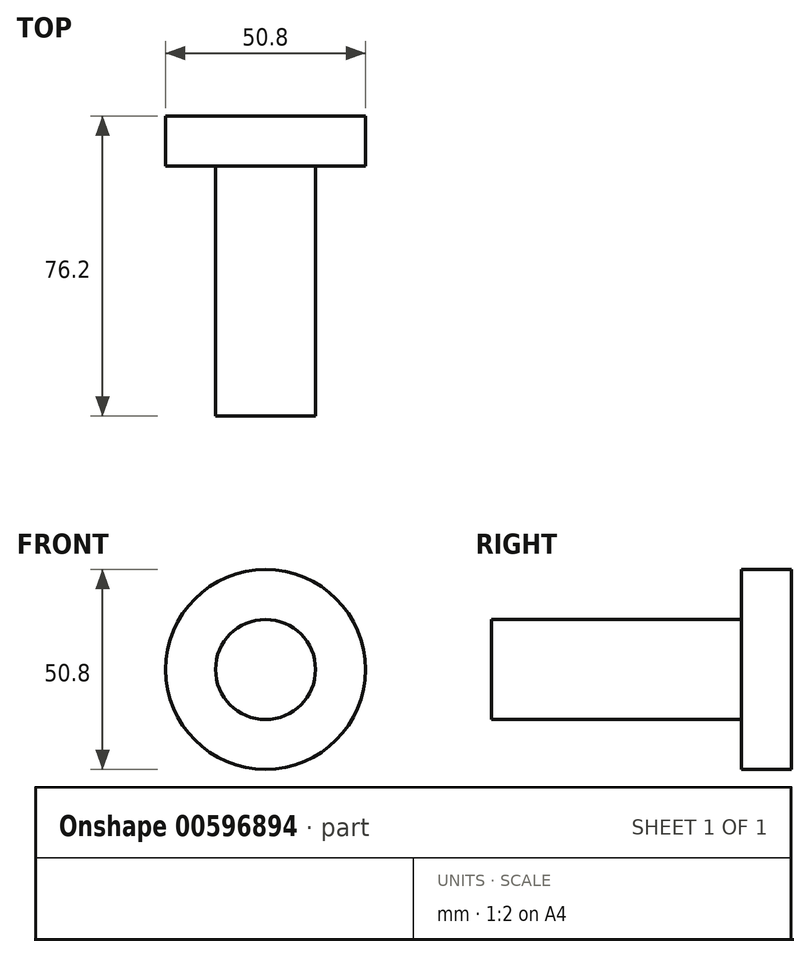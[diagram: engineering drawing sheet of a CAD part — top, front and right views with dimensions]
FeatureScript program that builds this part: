
annotation { "Feature Type Name" : "Feature", "Feature Type Description" : "" }
export const myFeature = defineFeature(function(context is Context, id is Id, definition is map)
    precondition{}
    {
        {
            var Q0;
            Q0=qCreatedBy(makeId("Top.planeOp"),FACE);
            var sketch = newSketch(context, id + "F0", { "sketchPlane" : qUnion([Q0])});
            skLineSegment(sketch, "E0", {"start": v(0, 76.2) * mm, "end": v(0, 0) * mm});
            skLineSegment(sketch, "E1", {"start": v(0, 0) * mm, "end": v(12.7, 0) * mm});
            skLineSegment(sketch, "E2", {"start": v(12.7, 0) * mm, "end": v(12.7, 63.5) * mm});
            skLineSegment(sketch, "E3", {"start": v(12.7, 63.5) * mm, "end": v(25.4, 63.5) * mm});
            skLineSegment(sketch, "E4", {"start": v(25.4, 63.5) * mm, "end": v(25.4, 76.2) * mm});
            skLineSegment(sketch, "E5", {"start": v(25.4, 76.2) * mm, "end": v(0, 76.2) * mm});
            skSolve(sketch);
        }
        {
            var Q0;
            Q0 = qSketchRegion(id + "F0", true);
            var Q1;
            Q1=sQuery(id+"F0.wireOp",EDGE,"E0");
            revolve(context, id + "F1", {"entities" : qUnion([Q0]), "axis" : qUnion([Q1]), "revolveType" : RevolveType.FULL});
        }
    });
